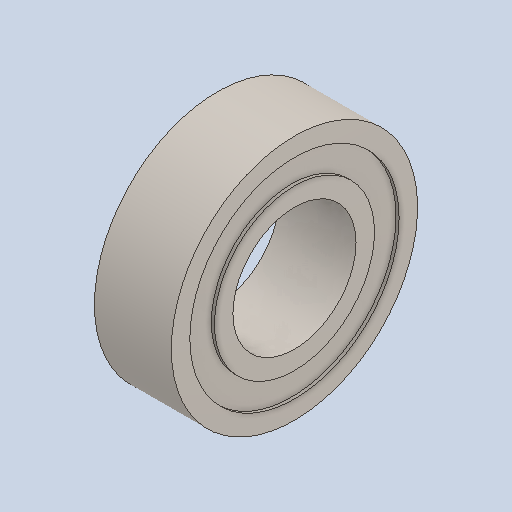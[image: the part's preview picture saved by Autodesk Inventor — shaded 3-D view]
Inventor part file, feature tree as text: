
AUTODESK INVENTOR PART (.ipt)
format: ipt  version: 2023.2 (Build 272271000, 271)  size: 134,144 bytes
history: native  units: in
note: dims shown in document units (in); Inventor stores cm internally (conversion verified against a paired STEP export)
features: revolve x1
ambient origin geometry x8: Origin, YZ Plane, XZ Plane, XY Plane, X Axis, Y Axis, Z Axis, Center Point
bodies: Solid1 (feature_tree)
feature tree (1):
  revolve  "Revolve1"  [1 undecoded]
note: 1 required parameter value undecoded (feature->parameter linkage not recoverable at this tier; creation-order binding heuristic only, values carry confidence <= 0.55)
